# Revit family: ge-t552_50Hz_1
name_source: partatom
category: Plumbing Fixtures
units: mm (PartAtom-declared; Revit-internal decimal feet)

## family parameters
Always vertical = Yes
Cut with Voids When Loaded = No
OmniClass Number = 23.75.10.17.17.11
OmniClass Title = Heat Pumps, Heating Function
Part Type = Normal
Room Calculation Point = No
Round Connector Dimension = Use Diameter
Shared = No
Work Plane-Based = No

## types (4) — shared parameters
CW R3/4 = 27 mm
Clearance Front = 600 mm
Clearance Top = 200 mm  [stored 0.656168 ft]
Depth = 825 mm  [stored 2.70669 ft]
Description = 自然冷媒CO２小型業務用ヒートポンプ給湯機
FamilyVersion = ver1.6
H2 = 384 mm  [stored 1.25984 ft]
H3 = 167 mm  [stored 0.5479 ft]
Height = 2100 mm  [stored 6.88976 ft]
IfcExportAs = IfcPumpType
IfcExportType = USERDEFINED
L2 = 49 mm  [stored 0.160761 ft]
Manufacturer = 三菱電機株式会社
OmniClassCode = 23-33 17 11 11
URL = https://www.mitsubishielectric.co.jp
Uniclass2015Code = Pr_70_60_37_04
Uniclass2015Title = Air-to-water heat pumps
Uniclass2015Version = Systems v1.9
WD R3/4 = 27 mm
Width = 700 mm  [stored 2.29659 ft]
サービススペース = Yes
ユニット数 = 1
上水管径 = 22 mm
上水量 = 0.0 L
仕様書バージョン = Version1.0
企業コード = 108420
凍結防止ヒーター消費電力 = 0 kW
分類コード = 50056502300030
制御用消費電力 = 0 kW
即湯往き配管口 = 27 mm
即湯戻り配管口 = 27 mm
参照している仕様書等のバージョン = 公共建築工事標準仕様書（機械設備工事編）平成31年度版
吊り位置X = 550 mm
吊り位置Y = 575 mm
周波数 = 50 Hz
呼称 = ヒートポンプ給湯機
始動方式 = 直入
形式 = 業務用ヒートポンプ給湯機
排気配管 = No
排水管径 = 20 mm
排水配管 = No
推奨ブレーカー容量 = 30 A
最高給水圧力 = 0 kPa
極数 = 1
水配管 = No
法定耐用年数 = 15
消費電力 = 0 kW
混合給湯配管口 = 27 mm
温水入口温度_一次側 = 5 °C
温水出口温度_一次側 = 60 °C
温水配管 = No
積算_科目 = 8 給湯設備
符号 = WHP
給湯管径 = 22 mm
給湯能力 = 0 kW
製品リリース年月 = 2015/02/27
製品出荷対象 = 国内
設置方法 = 床置
負荷分類 = 1_熱源類
貯湯量 = 0.0 L
質量 = 0.00 kg
電動機出力_圧縮機 = 0 kW
電動機出力_送風機 = 0 kW
電圧 = 200 V
電圧_補機 = 0 V
電源種別 = 一般
高温給湯配管口 = 27 mm
高温給湯配管口_GET552H / 混合給湯配管口_GET552SU / 即湯往き配管口_GET552SUJ = 27 mm
zero-valued in all types: Clearance Back, Clearance Bottom, Clearance Left, Clearance Right, Cost, S寸法, ケーブルサイズ, 機械基礎_D, 機械基礎_H, 機械基礎_W, 機械基礎質量, 耐震強度, 騒音レベル(dB(A))

## per-type parameters (varying)
| type | H1 | L1 | L3 | 即湯往き配管口_Y/N | 即湯戻り配管口_Y/N | 最大電流値 | 最高使用圧力 | 構成品番 | 混合給湯配管口_Y/N | 減圧弁圧力 | 製品質量 | 運転質量 |
| 貯湯ユニット_GE-T552SUJ_三相 | 285 mm  [stored 0.935039 ft] | 53 mm  [stored 0.173885 ft] | 42 mm  [stored 0.137795 ft] | Yes | Yes | 12 A | 320.0 kPa | GE-T552SUJ | No | 280.0 kPa | 82.00 kg | 632.00 kg |
| 貯湯ユニット_GE-T552SU_三相 | 285 mm  [stored 0.935039 ft] | 53 mm  [stored 0.173885 ft] | 34.5 mm | Yes | No | 12 A | 320.0 kPa | GE-T552SU | No | 280.0 kPa | 81.00 kg | 631.00 kg |
| 貯湯ユニット_GE-T552_単相 | 250 mm  [stored 0.82021 ft] | 51 mm | 42 mm  [stored 0.137795 ft] | No | No | 19 A | 193.0 kPa | GE-T552 | Yes | 170.0 kPa | 76.00 kg | 626.00 kg |
| 貯湯ユニット_GE-T552H_単相 | 250 mm  [stored 0.82021 ft] | 51 mm | 42 mm  [stored 0.137795 ft] | Yes | No | 19 A | 193.0 kPa | GE-T552H | Yes | 170.0 kPa | 78.00 kg | 628.00 kg |

note: [stored X ft] marks values corroborated as IEEE doubles in the binary element streams (Revit-internal decimal feet)
